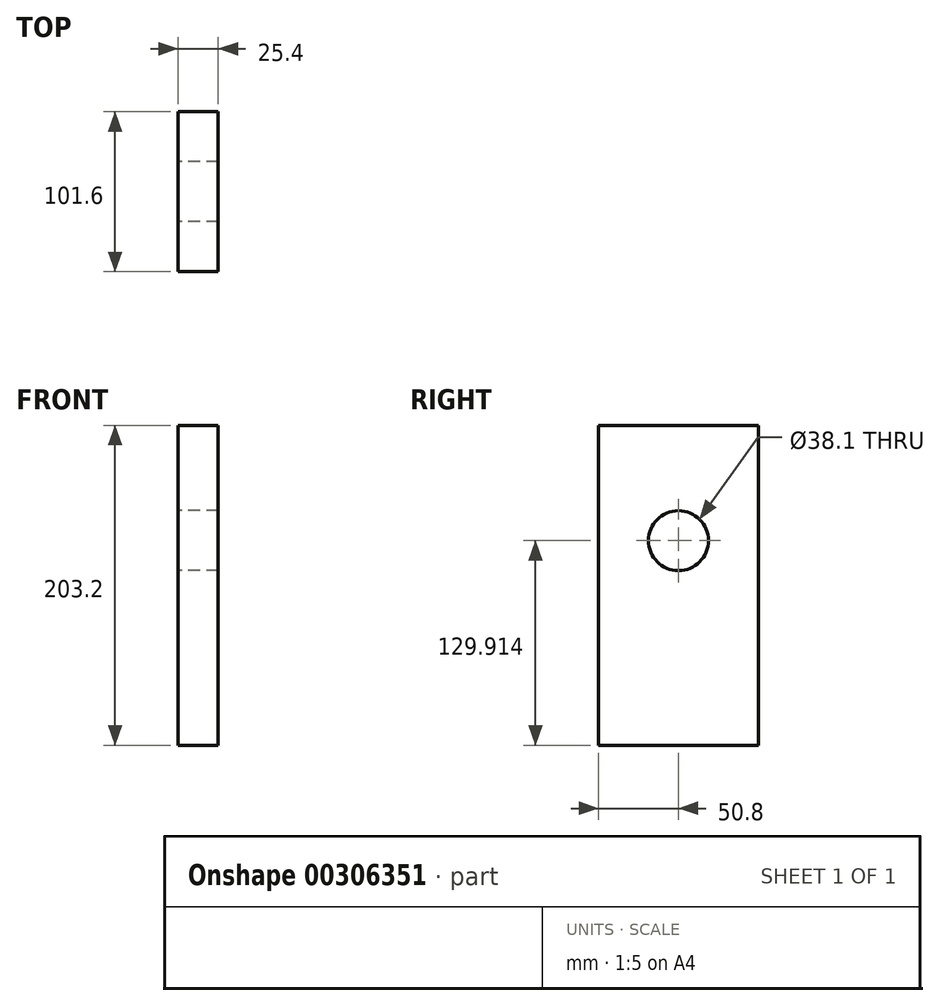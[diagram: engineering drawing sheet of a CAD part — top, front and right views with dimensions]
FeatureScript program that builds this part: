
annotation { "Feature Type Name" : "Feature", "Feature Type Description" : "" }
export const myFeature = defineFeature(function(context is Context, id is Id, definition is map)
    precondition{}
    {
        {
            var Q0;
            Q0=qCreatedBy(makeId("Right.planeOp"),FACE);
            var sketch = newSketch(context, id + "F0", { "sketchPlane" : qUnion([Q0])});
            skLineSegment(sketch, "E0.bottom", {"start": v(50.8, -101.6) * mm, "end": v(-50.8, -101.6) * mm});
            skLineSegment(sketch, "E0.top", {"start": v(50.8, 101.6) * mm, "end": v(-50.8, 101.6) * mm});
            skLineSegment(sketch, "E0.left", {"start": v(50.8, -101.6) * mm, "end": v(50.8, 101.6) * mm});
            skLineSegment(sketch, "E0.right", {"start": v(-50.8, -101.6) * mm, "end": v(-50.8, 101.6) * mm});
            skPoint(sketch, "E0.middle", {"position": v(0, 0) * mm});
            skCircle(sketch, "E1", {"center": v(0, 28.31) * mm, "radius": 19.05 * mm});
            skLineSegment(sketch, "E2.bottom", {"start": v(-50.8, 101.6) * mm, "end": v(50.8, 101.6) * mm});
            skLineSegment(sketch, "E2.top", {"start": v(-50.8, 151.7) * mm, "end": v(50.8, 151.7) * mm});
            skLineSegment(sketch, "E2.left", {"start": v(-50.8, 101.6) * mm, "end": v(-50.8, 151.7) * mm});
            skLineSegment(sketch, "E2.right", {"start": v(50.8, 101.6) * mm, "end": v(50.8, 151.7) * mm});
            skLineSegment(sketch, "E3", {"start": v(0, 151.7) * mm, "end": v(-50.8, 101.6) * mm});
            skLineSegment(sketch, "E4", {"start": v(0, 151.7) * mm, "end": v(50.8, 101.6) * mm});
            skSolve(sketch);
        }
        {
            var Q0;
            {var subQ0=sQuery(id+"F0.wireOp",EDGE,"E2.bottom");Q0=makeQuery(id+"F0.imprint","IMPRINT",FACE,{"disambiguationData":[TD([[makeQuery(id+"F0.imprint","IMPRINT",EDGE,{"derivedFrom":subQ0}),1.0]])]});}
            var Q1;
            Q1=makeQuery(id+"F0.imprint","IMPRINT",FACE,{"disambiguationData":[TD([[makeQuery(id+"F0.imprint","IMPRINT",EDGE,{"derivedFrom":sQuery(id+"F0.wireOp",EDGE,"E0.bottom")}),-1.0]])]});
            extrude(context, id + "F1", {"entities" : qUnion([Q0, Q1]), "depth" : 25.4 * mm});
        }
    });
